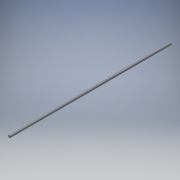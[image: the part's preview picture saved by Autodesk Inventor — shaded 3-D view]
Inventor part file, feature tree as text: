
AUTODESK INVENTOR PART (.ipt)
format: ipt  version: 2018 (Build 220112000, 112)  size: 93,696 bytes
history: native  units: in
note: dims shown in document units (in); Inventor stores cm internally (conversion verified against a paired STEP export)
features: revolve x1, sketch x1
ambient origin geometry x8: Origin, YZ Plane, XZ Plane, XY Plane, X Axis, Y Axis, Z Axis, Center Point
bodies: Solid1 (feature_tree)
feature tree (2):
  revolve  "Revolution1"  [1 undecoded]
  sketch  "Sketch1"  dims[d0=0.1575in d1=19.685in d2=90.0deg]
note: 1 required parameter value undecoded (feature->parameter linkage not recoverable at this tier; creation-order binding heuristic only, values carry confidence <= 0.55)
